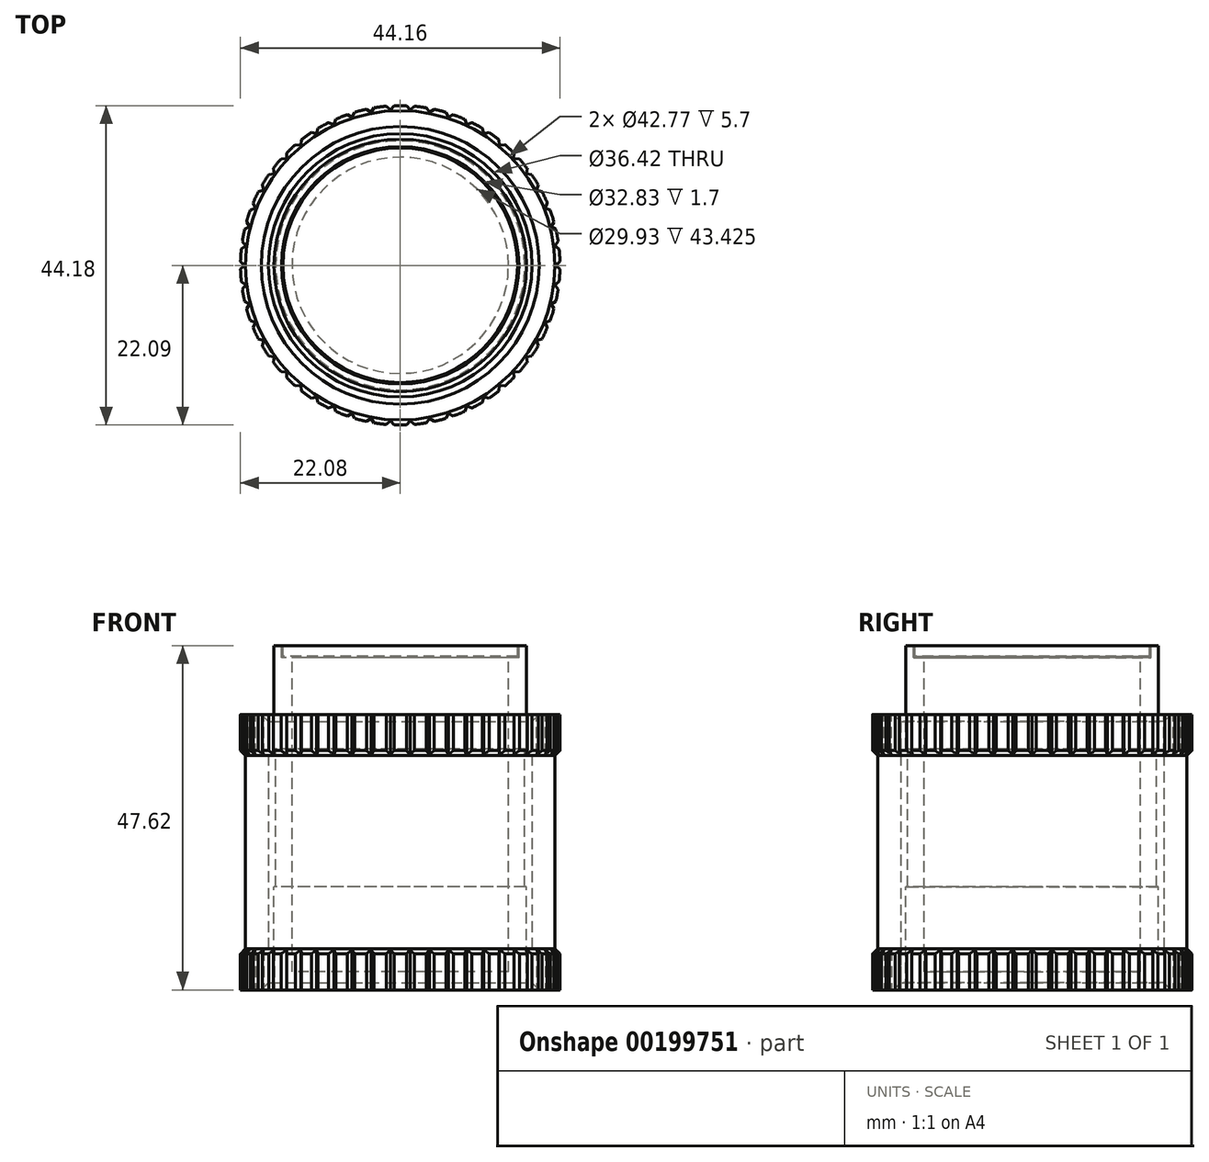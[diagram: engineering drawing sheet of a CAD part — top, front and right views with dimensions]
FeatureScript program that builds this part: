
annotation { "Feature Type Name" : "Feature", "Feature Type Description" : "" }
export const myFeature = defineFeature(function(context is Context, id is Id, definition is map)
    precondition{}
    {
        {
            var Q0;
            Q0=qCreatedBy(makeId("Front.planeOp"),FACE);
            var sketch = newSketch(context, id + "F0", { "sketchPlane" : qUnion([Q0])});
            skLineSegment(sketch, "E0", {"start": v(0, 33.65) * mm, "end": v(0, -36.31) * mm, "construction": true});
            skLineSegment(sketch, "E1", {"start": v(0, 23.81) * mm, "end": v(-17.46, 23.81) * mm});
            skLineSegment(sketch, "E2", {"start": v(-17.46, 23.81) * mm, "end": v(-17.46, -23.81) * mm});
            skLineSegment(sketch, "E3", {"start": v(-17.46, -23.81) * mm, "end": v(0, -23.81) * mm});
            skPoint(sketch, "E4", {"position": v(-17.46, 0) * mm});
            skLineSegment(sketch, "E5.bottom", {"start": v(-17.46, 9.53) * mm, "end": v(-17.21, 9.53) * mm});
            skLineSegment(sketch, "E5.top", {"start": v(-17.46, -9.52) * mm, "end": v(-17.21, -9.52) * mm});
            skLineSegment(sketch, "E5.left", {"start": v(-17.46, 9.52) * mm, "end": v(-17.46, -9.52) * mm});
            skLineSegment(sketch, "E5.right", {"start": v(-17.21, 9.52) * mm, "end": v(-17.21, -9.52) * mm});
            skLineSegment(sketch, "E6", {"start": v(-14.96, 23.81) * mm, "end": v(-14.96, -21.31) * mm});
            skLineSegment(sketch, "E7", {"start": v(-14.96, -21.31) * mm, "end": v(0, -21.31) * mm});
            skPoint(sketch, "E7.endSnap0", {"position": v(0, -1.33) * mm});
            skLineSegment(sketch, "E8", {"start": v(0, -23.81) * mm, "end": v(0, -21.31) * mm});
            skSolve(sketch);
        }
        {
            var Q0;
            {var subQ0=sQuery(id+"F0.wireOp",EDGE,"E3");Q0=makeQuery(id+"F0.imprint","IMPRINT",FACE,{"disambiguationData":[TD([[makeQuery(id+"F0.imprint","IMPRINT",EDGE,{"derivedFrom":subQ0}),1.0]])]});}
            var Q1;
            Q1=sQuery(id+"F0.wireOp",EDGE,"E0");
            revolve(context, id + "F1", {"entities" : qUnion([Q0]), "axis" : qUnion([Q1]), "revolveType" : RevolveType.FULL});
        }
        {
            var Q0;
            Q0=makeQuery(id+"F1.opRevolve","SWEPT_FACE",FACE,{"disambiguationData":[OSD([sQuery(id+"F0.wireOp",EDGE,"E1")])]});
            cPlane(context, id + "F2", {"entities" : qUnion([Q0]), "cplaneType" : CPlaneType.OFFSET, "offset" : 0 * mm, "width" : 150 * mm, "height" : 150 * mm});
        }
        {
            var Q0;
            Q0=qCreatedBy(id+"F2.planeOp",FACE);
            var sketch = newSketch(context, id + "F3", { "sketchPlane" : qUnion([Q0])});
            skCircle(sketch, "E9", {"center": v(0, 0) * mm, "radius": 16.21 * mm});
            skPoint(sketch, "E10", {"position": v(-17.46, 0) * mm});
            skSolve(sketch);
        }
        {
            var Q0;
            Q0 = qSketchRegion(id + "F3", true);
            extrude(context, id + "F4", {"entities" : qUnion([Q0]), "oppositeDirection" : true, "depth" : 1.5 * mm});
        }
        {
            var Q0;
            Q0=makeQuery(id+"F4.opExtrude","SWEPT_BODY",BODY,{"disambiguationData":[OSD([sQuery(id+"F3.wireOp",EDGE,"E9")])]});
            var Q1;
            Q1=makeQuery(id+"F1.opRevolve","SWEPT_BODY",BODY,{"disambiguationData":[OSD([sQuery(id+"F0.wireOp",EDGE,"E1"),sQuery(id+"F0.wireOp",EDGE,"E2"),sQuery(id+"F0.wireOp",EDGE,"E3"),sQuery(id+"F0.wireOp",EDGE,"E5.bottom"),sQuery(id+"F0.wireOp",EDGE,"E5.top"),sQuery(id+"F0.wireOp",EDGE,"E5.right"),sQuery(id+"F0.wireOp",EDGE,"E6"),sQuery(id+"F0.wireOp",EDGE,"E7"),sQuery(id+"F0.wireOp",EDGE,"E8")])]});
            booleanBodies(context, id + "F5", {"operationType" : BooleanOperationType.SUBTRACTION, "tools" : qUnion([Q0]), "targets" : qUnion([Q1]), "offset" : true, "offsetAll" : true, "offsetDistance" : .2 * mm, "keepTools" : true});
        }
        {
            var Q0;
            Q0=makeQuery(id+"F1.opRevolve","SWEPT_FACE",FACE,{"disambiguationData":[OSD([sQuery(id+"F0.wireOp",EDGE,"E3")])]});
            cPlane(context, id + "F6", {"entities" : qUnion([Q0]), "cplaneType" : CPlaneType.OFFSET, "offset" : 0 * mm, "width" : 150 * mm, "height" : 150 * mm});
        }
        {
            var Q0;
            Q0=qCreatedBy(id+"F6.planeOp",FACE);
            var sketch = newSketch(context, id + "F7", { "sketchPlane" : qUnion([Q0])});
            skCircle(sketch, "E11", {"center": v(0, 0) * mm, "radius": 18.21 * mm});
            skCircle(sketch, "E12", {"center": v(0, 0) * mm, "radius": 21.39 * mm});
            skSolve(sketch);
        }
        {
            var Q0;
            Q0=makeQuery(id+"F7.imprint","IMPRINT",FACE,{"disambiguationData":[TD([[makeQuery(id+"F7.imprint","IMPRINT",EDGE,{"derivedFrom":sQuery(id+"F7.wireOp",EDGE,"E11")}),-1.0]])]});
            extrude(context, id + "F8", {"entities" : qUnion([Q0]), "oppositeDirection" : true, "depth" : 38.1 * mm, "offsetDistance" : 25 * mm});
        }
        {
            var Q0;
            Q0=qCreatedBy(makeId("Front.planeOp"),FACE);
            var sketch = newSketch(context, id + "F9", { "sketchPlane" : qUnion([Q0])});
            skLineSegment(sketch, "E13", {"start": v(-21.39, -23.81) * mm, "end": v(-21.39, 14.29) * mm});
            skLineSegment(sketch, "E14.0", {"start": v(21.39, 14.29) * mm, "end": v(-21.39, 14.29) * mm});
            skLineSegment(sketch, "E15", {"start": v(-21.39, 14.29) * mm, "end": v(-22.09, 14.29) * mm});
            skLineSegment(sketch, "E16", {"start": v(-22.09, 14.29) * mm, "end": v(-22.09, 9.29) * mm});
            skLineSegment(sketch, "E17", {"start": v(-22.09, 9.29) * mm, "end": v(-21.39, 8.59) * mm});
            skLineSegment(sketch, "E18", {"start": v(0, 29.24) * mm, "end": v(0, -34.18) * mm, "construction": true});
            skLineSegment(sketch, "E19", {"start": v(-37.39, -4.76) * mm, "end": v(45.58, -4.76) * mm, "construction": true});
            skPoint(sketch, "E20", {"position": v(-21.39, -4.76) * mm});
            skSolve(sketch);
        }
        {
            var Q0;
            {var subQ0=sQuery(id+"F9.wireOp",EDGE,"E15");Q0=makeQuery(id+"F9.imprint","IMPRINT",FACE,{"disambiguationData":[TD([[makeQuery(id+"F9.imprint","IMPRINT",EDGE,{"derivedFrom":subQ0}),1.0]])]});}
            var Q1;
            Q1=sQuery(id+"F9.wireOp",EDGE,"E18");
            revolve(context, id + "F10", {"surfaceOperationType" : NewSurfaceOperationType.NEW, "entities" : qUnion([Q0]), "axis" : qUnion([Q1]), "revolveType" : RevolveType.FULL});
        }
        {
            var Q0;
            Q0=qCreatedBy(makeId("Top.planeOp"),FACE);
            var Q1;
            Q1=sQuery(id+"F9.wireOp",VERTEX,"E20");
            cPlane(context, id + "F11", {"entities" : qUnion([Q0, Q1]), "cplaneType" : CPlaneType.PLANE_POINT, "offset" : 25 * mm, "width" : 150 * mm, "height" : 150 * mm});
        }
        {
            var Q0;
            Q0=makeQuery(id+"F10.opRevolve","SWEPT_FACE",FACE,{"disambiguationData":[OSD([sQuery(id+"F9.wireOp",EDGE,"E15")])]});
            cPlane(context, id + "F12", {"entities" : qUnion([Q0]), "cplaneType" : CPlaneType.OFFSET, "offset" : 0 * mm, "width" : 150 * mm, "height" : 150 * mm});
        }
        {
            var Q0;
            Q0=qCreatedBy(id+"F12.planeOp",FACE);
            var sketch = newSketch(context, id + "F13", { "sketchPlane" : qUnion([Q0])});
            skLineSegment(sketch, "E21", {"start": v(27.17, 0) * mm, "end": v(-30.77, 0) * mm, "construction": true});
            skLineSegment(sketch, "E22.bottom", {"start": v(-22.6, 1.06) * mm, "end": v(-21.54, 0) * mm});
            skLineSegment(sketch, "E22.top", {"start": v(-23.66, 0) * mm, "end": v(-22.6, -1.06) * mm});
            skLineSegment(sketch, "E22.left", {"start": v(-22.6, 1.06) * mm, "end": v(-23.66, 0) * mm});
            skLineSegment(sketch, "E22.right", {"start": v(-21.54, 0) * mm, "end": v(-22.6, -1.06) * mm});
            skPoint(sketch, "E23", {"position": v(-22.09, 0) * mm});
            skSolve(sketch);
        }
        {
            var Q0;
            Q0=makeQuery(id+"F13.imprint","IMPRINT",FACE,{"disambiguationData":[TD([[makeQuery(id+"F13.imprint","IMPRINT",EDGE,{"derivedFrom":sQuery(id+"F13.wireOp",EDGE,"E22.bottom")}),-1.0]])]});
            var Q1;
            Q1=makeQuery(id+"F10.opRevolve","SWEPT_FACE",FACE,{"disambiguationData":[OSD([sQuery(id+"F9.wireOp",EDGE,"E17")])]});
            extrude(context, id + "F14", {"entities" : qUnion([Q0]), "endBound" : BoundingType.UP_TO_SURFACE, "oppositeDirection" : true, "depth" : 25 * mm, "endBoundEntityFace" : qUnion([Q1]), "offsetDistance" : 25 * mm});
        }
        {
            var Q0;
            Q0=qCreatedBy(makeId("Front.planeOp"),FACE);
            var sketch = newSketch(context, id + "F15", { "sketchPlane" : qUnion([Q0])});
            skLineSegment(sketch, "E24", {"start": v(0, 30.02) * mm, "end": v(0, -34.27) * mm, "construction": true});
            skSolve(sketch);
        }
        {
            var Q0;
            Q0=makeQuery(id+"F14.opExtrude","SWEPT_BODY",BODY,{"disambiguationData":[OSD([sQuery(id+"F13.wireOp",EDGE,"E22.bottom"),sQuery(id+"F13.wireOp",EDGE,"E22.top"),sQuery(id+"F13.wireOp",EDGE,"E22.left"),sQuery(id+"F13.wireOp",EDGE,"E22.right")])]});
            var Q1;
            Q1=sQuery(id+"F15.wireOp",EDGE,"E24");
            circularPattern(context, id + "F16", {"entities" : qUnion([Q0]), "axis" : qUnion([Q1]), "angle" : 360 * degree, "instanceCount" : 50, "equalSpace" : true});
        }
        {
            var Q0;
            Q0=makeQuery(id+"F14.opExtrude","SWEPT_BODY",BODY,{"disambiguationData":[OSD([sQuery(id+"F13.wireOp",EDGE,"E22.bottom"),sQuery(id+"F13.wireOp",EDGE,"E22.top"),sQuery(id+"F13.wireOp",EDGE,"E22.left"),sQuery(id+"F13.wireOp",EDGE,"E22.right")])]});
            var Q1;
            Q1=makeQuery(id+"F16.opPattern","COPY",BODY,{"derivedFrom":makeQuery(id+"F14.opExtrude","SWEPT_BODY",BODY,{"disambiguationData":[OSD([sQuery(id+"F13.wireOp",EDGE,"E22.bottom"),sQuery(id+"F13.wireOp",EDGE,"E22.top"),sQuery(id+"F13.wireOp",EDGE,"E22.left"),sQuery(id+"F13.wireOp",EDGE,"E22.right")])]}),"instanceName":"1"});
            var Q2;
            Q2=makeQuery(id+"F16.opPattern","COPY",BODY,{"derivedFrom":makeQuery(id+"F14.opExtrude","SWEPT_BODY",BODY,{"disambiguationData":[OSD([sQuery(id+"F13.wireOp",EDGE,"E22.bottom"),sQuery(id+"F13.wireOp",EDGE,"E22.top"),sQuery(id+"F13.wireOp",EDGE,"E22.left"),sQuery(id+"F13.wireOp",EDGE,"E22.right")])]}),"instanceName":"2"});
            var Q3;
            Q3=makeQuery(id+"F16.opPattern","COPY",BODY,{"derivedFrom":makeQuery(id+"F14.opExtrude","SWEPT_BODY",BODY,{"disambiguationData":[OSD([sQuery(id+"F13.wireOp",EDGE,"E22.bottom"),sQuery(id+"F13.wireOp",EDGE,"E22.top"),sQuery(id+"F13.wireOp",EDGE,"E22.left"),sQuery(id+"F13.wireOp",EDGE,"E22.right")])]}),"instanceName":"3"});
            var Q4;
            Q4=makeQuery(id+"F16.opPattern","COPY",BODY,{"derivedFrom":makeQuery(id+"F14.opExtrude","SWEPT_BODY",BODY,{"disambiguationData":[OSD([sQuery(id+"F13.wireOp",EDGE,"E22.bottom"),sQuery(id+"F13.wireOp",EDGE,"E22.top"),sQuery(id+"F13.wireOp",EDGE,"E22.left"),sQuery(id+"F13.wireOp",EDGE,"E22.right")])]}),"instanceName":"4"});
            var Q5;
            Q5=makeQuery(id+"F16.opPattern","COPY",BODY,{"derivedFrom":makeQuery(id+"F14.opExtrude","SWEPT_BODY",BODY,{"disambiguationData":[OSD([sQuery(id+"F13.wireOp",EDGE,"E22.bottom"),sQuery(id+"F13.wireOp",EDGE,"E22.top"),sQuery(id+"F13.wireOp",EDGE,"E22.left"),sQuery(id+"F13.wireOp",EDGE,"E22.right")])]}),"instanceName":"5"});
            var Q6;
            Q6=makeQuery(id+"F16.opPattern","COPY",BODY,{"derivedFrom":makeQuery(id+"F14.opExtrude","SWEPT_BODY",BODY,{"disambiguationData":[OSD([sQuery(id+"F13.wireOp",EDGE,"E22.bottom"),sQuery(id+"F13.wireOp",EDGE,"E22.top"),sQuery(id+"F13.wireOp",EDGE,"E22.left"),sQuery(id+"F13.wireOp",EDGE,"E22.right")])]}),"instanceName":"6"});
            var Q7;
            Q7=makeQuery(id+"F16.opPattern","COPY",BODY,{"derivedFrom":makeQuery(id+"F14.opExtrude","SWEPT_BODY",BODY,{"disambiguationData":[OSD([sQuery(id+"F13.wireOp",EDGE,"E22.bottom"),sQuery(id+"F13.wireOp",EDGE,"E22.top"),sQuery(id+"F13.wireOp",EDGE,"E22.left"),sQuery(id+"F13.wireOp",EDGE,"E22.right")])]}),"instanceName":"7"});
            var Q8;
            Q8=makeQuery(id+"F16.opPattern","COPY",BODY,{"derivedFrom":makeQuery(id+"F14.opExtrude","SWEPT_BODY",BODY,{"disambiguationData":[OSD([sQuery(id+"F13.wireOp",EDGE,"E22.bottom"),sQuery(id+"F13.wireOp",EDGE,"E22.top"),sQuery(id+"F13.wireOp",EDGE,"E22.left"),sQuery(id+"F13.wireOp",EDGE,"E22.right")])]}),"instanceName":"8"});
            var Q9;
            Q9=makeQuery(id+"F16.opPattern","COPY",BODY,{"derivedFrom":makeQuery(id+"F14.opExtrude","SWEPT_BODY",BODY,{"disambiguationData":[OSD([sQuery(id+"F13.wireOp",EDGE,"E22.bottom"),sQuery(id+"F13.wireOp",EDGE,"E22.top"),sQuery(id+"F13.wireOp",EDGE,"E22.left"),sQuery(id+"F13.wireOp",EDGE,"E22.right")])]}),"instanceName":"9"});
            var Q10;
            Q10=makeQuery(id+"F16.opPattern","COPY",BODY,{"derivedFrom":makeQuery(id+"F14.opExtrude","SWEPT_BODY",BODY,{"disambiguationData":[OSD([sQuery(id+"F13.wireOp",EDGE,"E22.bottom"),sQuery(id+"F13.wireOp",EDGE,"E22.top"),sQuery(id+"F13.wireOp",EDGE,"E22.left"),sQuery(id+"F13.wireOp",EDGE,"E22.right")])]}),"instanceName":"10"});
            var Q11;
            Q11=makeQuery(id+"F16.opPattern","COPY",BODY,{"derivedFrom":makeQuery(id+"F14.opExtrude","SWEPT_BODY",BODY,{"disambiguationData":[OSD([sQuery(id+"F13.wireOp",EDGE,"E22.bottom"),sQuery(id+"F13.wireOp",EDGE,"E22.top"),sQuery(id+"F13.wireOp",EDGE,"E22.left"),sQuery(id+"F13.wireOp",EDGE,"E22.right")])]}),"instanceName":"11"});
            var Q12;
            Q12=makeQuery(id+"F16.opPattern","COPY",BODY,{"derivedFrom":makeQuery(id+"F14.opExtrude","SWEPT_BODY",BODY,{"disambiguationData":[OSD([sQuery(id+"F13.wireOp",EDGE,"E22.bottom"),sQuery(id+"F13.wireOp",EDGE,"E22.top"),sQuery(id+"F13.wireOp",EDGE,"E22.left"),sQuery(id+"F13.wireOp",EDGE,"E22.right")])]}),"instanceName":"12"});
            var Q13;
            Q13=makeQuery(id+"F16.opPattern","COPY",BODY,{"derivedFrom":makeQuery(id+"F14.opExtrude","SWEPT_BODY",BODY,{"disambiguationData":[OSD([sQuery(id+"F13.wireOp",EDGE,"E22.bottom"),sQuery(id+"F13.wireOp",EDGE,"E22.top"),sQuery(id+"F13.wireOp",EDGE,"E22.left"),sQuery(id+"F13.wireOp",EDGE,"E22.right")])]}),"instanceName":"13"});
            var Q14;
            Q14=makeQuery(id+"F16.opPattern","COPY",BODY,{"derivedFrom":makeQuery(id+"F14.opExtrude","SWEPT_BODY",BODY,{"disambiguationData":[OSD([sQuery(id+"F13.wireOp",EDGE,"E22.bottom"),sQuery(id+"F13.wireOp",EDGE,"E22.top"),sQuery(id+"F13.wireOp",EDGE,"E22.left"),sQuery(id+"F13.wireOp",EDGE,"E22.right")])]}),"instanceName":"14"});
            var Q15;
            Q15=makeQuery(id+"F16.opPattern","COPY",BODY,{"derivedFrom":makeQuery(id+"F14.opExtrude","SWEPT_BODY",BODY,{"disambiguationData":[OSD([sQuery(id+"F13.wireOp",EDGE,"E22.bottom"),sQuery(id+"F13.wireOp",EDGE,"E22.top"),sQuery(id+"F13.wireOp",EDGE,"E22.left"),sQuery(id+"F13.wireOp",EDGE,"E22.right")])]}),"instanceName":"15"});
            var Q16;
            Q16=makeQuery(id+"F16.opPattern","COPY",BODY,{"derivedFrom":makeQuery(id+"F14.opExtrude","SWEPT_BODY",BODY,{"disambiguationData":[OSD([sQuery(id+"F13.wireOp",EDGE,"E22.bottom"),sQuery(id+"F13.wireOp",EDGE,"E22.top"),sQuery(id+"F13.wireOp",EDGE,"E22.left"),sQuery(id+"F13.wireOp",EDGE,"E22.right")])]}),"instanceName":"16"});
            var Q17;
            Q17=makeQuery(id+"F16.opPattern","COPY",BODY,{"derivedFrom":makeQuery(id+"F14.opExtrude","SWEPT_BODY",BODY,{"disambiguationData":[OSD([sQuery(id+"F13.wireOp",EDGE,"E22.bottom"),sQuery(id+"F13.wireOp",EDGE,"E22.top"),sQuery(id+"F13.wireOp",EDGE,"E22.left"),sQuery(id+"F13.wireOp",EDGE,"E22.right")])]}),"instanceName":"17"});
            var Q18;
            Q18=makeQuery(id+"F16.opPattern","COPY",BODY,{"derivedFrom":makeQuery(id+"F14.opExtrude","SWEPT_BODY",BODY,{"disambiguationData":[OSD([sQuery(id+"F13.wireOp",EDGE,"E22.bottom"),sQuery(id+"F13.wireOp",EDGE,"E22.top"),sQuery(id+"F13.wireOp",EDGE,"E22.left"),sQuery(id+"F13.wireOp",EDGE,"E22.right")])]}),"instanceName":"18"});
            var Q19;
            Q19=makeQuery(id+"F16.opPattern","COPY",BODY,{"derivedFrom":makeQuery(id+"F14.opExtrude","SWEPT_BODY",BODY,{"disambiguationData":[OSD([sQuery(id+"F13.wireOp",EDGE,"E22.bottom"),sQuery(id+"F13.wireOp",EDGE,"E22.top"),sQuery(id+"F13.wireOp",EDGE,"E22.left"),sQuery(id+"F13.wireOp",EDGE,"E22.right")])]}),"instanceName":"19"});
            var Q20;
            Q20=makeQuery(id+"F16.opPattern","COPY",BODY,{"derivedFrom":makeQuery(id+"F14.opExtrude","SWEPT_BODY",BODY,{"disambiguationData":[OSD([sQuery(id+"F13.wireOp",EDGE,"E22.bottom"),sQuery(id+"F13.wireOp",EDGE,"E22.top"),sQuery(id+"F13.wireOp",EDGE,"E22.left"),sQuery(id+"F13.wireOp",EDGE,"E22.right")])]}),"instanceName":"20"});
            var Q21;
            Q21=makeQuery(id+"F16.opPattern","COPY",BODY,{"derivedFrom":makeQuery(id+"F14.opExtrude","SWEPT_BODY",BODY,{"disambiguationData":[OSD([sQuery(id+"F13.wireOp",EDGE,"E22.bottom"),sQuery(id+"F13.wireOp",EDGE,"E22.top"),sQuery(id+"F13.wireOp",EDGE,"E22.left"),sQuery(id+"F13.wireOp",EDGE,"E22.right")])]}),"instanceName":"21"});
            var Q22;
            Q22=makeQuery(id+"F16.opPattern","COPY",BODY,{"derivedFrom":makeQuery(id+"F14.opExtrude","SWEPT_BODY",BODY,{"disambiguationData":[OSD([sQuery(id+"F13.wireOp",EDGE,"E22.bottom"),sQuery(id+"F13.wireOp",EDGE,"E22.top"),sQuery(id+"F13.wireOp",EDGE,"E22.left"),sQuery(id+"F13.wireOp",EDGE,"E22.right")])]}),"instanceName":"22"});
            var Q23;
            Q23=makeQuery(id+"F16.opPattern","COPY",BODY,{"derivedFrom":makeQuery(id+"F14.opExtrude","SWEPT_BODY",BODY,{"disambiguationData":[OSD([sQuery(id+"F13.wireOp",EDGE,"E22.bottom"),sQuery(id+"F13.wireOp",EDGE,"E22.top"),sQuery(id+"F13.wireOp",EDGE,"E22.left"),sQuery(id+"F13.wireOp",EDGE,"E22.right")])]}),"instanceName":"23"});
            var Q24;
            Q24=makeQuery(id+"F16.opPattern","COPY",BODY,{"derivedFrom":makeQuery(id+"F14.opExtrude","SWEPT_BODY",BODY,{"disambiguationData":[OSD([sQuery(id+"F13.wireOp",EDGE,"E22.bottom"),sQuery(id+"F13.wireOp",EDGE,"E22.top"),sQuery(id+"F13.wireOp",EDGE,"E22.left"),sQuery(id+"F13.wireOp",EDGE,"E22.right")])]}),"instanceName":"24"});
            var Q25;
            Q25=makeQuery(id+"F16.opPattern","COPY",BODY,{"derivedFrom":makeQuery(id+"F14.opExtrude","SWEPT_BODY",BODY,{"disambiguationData":[OSD([sQuery(id+"F13.wireOp",EDGE,"E22.bottom"),sQuery(id+"F13.wireOp",EDGE,"E22.top"),sQuery(id+"F13.wireOp",EDGE,"E22.left"),sQuery(id+"F13.wireOp",EDGE,"E22.right")])]}),"instanceName":"25"});
            var Q26;
            Q26=makeQuery(id+"F16.opPattern","COPY",BODY,{"derivedFrom":makeQuery(id+"F14.opExtrude","SWEPT_BODY",BODY,{"disambiguationData":[OSD([sQuery(id+"F13.wireOp",EDGE,"E22.bottom"),sQuery(id+"F13.wireOp",EDGE,"E22.top"),sQuery(id+"F13.wireOp",EDGE,"E22.left"),sQuery(id+"F13.wireOp",EDGE,"E22.right")])]}),"instanceName":"26"});
            var Q27;
            Q27=makeQuery(id+"F16.opPattern","COPY",BODY,{"derivedFrom":makeQuery(id+"F14.opExtrude","SWEPT_BODY",BODY,{"disambiguationData":[OSD([sQuery(id+"F13.wireOp",EDGE,"E22.bottom"),sQuery(id+"F13.wireOp",EDGE,"E22.top"),sQuery(id+"F13.wireOp",EDGE,"E22.left"),sQuery(id+"F13.wireOp",EDGE,"E22.right")])]}),"instanceName":"27"});
            var Q28;
            Q28=makeQuery(id+"F16.opPattern","COPY",BODY,{"derivedFrom":makeQuery(id+"F14.opExtrude","SWEPT_BODY",BODY,{"disambiguationData":[OSD([sQuery(id+"F13.wireOp",EDGE,"E22.bottom"),sQuery(id+"F13.wireOp",EDGE,"E22.top"),sQuery(id+"F13.wireOp",EDGE,"E22.left"),sQuery(id+"F13.wireOp",EDGE,"E22.right")])]}),"instanceName":"28"});
            var Q29;
            Q29=makeQuery(id+"F16.opPattern","COPY",BODY,{"derivedFrom":makeQuery(id+"F14.opExtrude","SWEPT_BODY",BODY,{"disambiguationData":[OSD([sQuery(id+"F13.wireOp",EDGE,"E22.bottom"),sQuery(id+"F13.wireOp",EDGE,"E22.top"),sQuery(id+"F13.wireOp",EDGE,"E22.left"),sQuery(id+"F13.wireOp",EDGE,"E22.right")])]}),"instanceName":"29"});
            var Q30;
            Q30=makeQuery(id+"F16.opPattern","COPY",BODY,{"derivedFrom":makeQuery(id+"F14.opExtrude","SWEPT_BODY",BODY,{"disambiguationData":[OSD([sQuery(id+"F13.wireOp",EDGE,"E22.bottom"),sQuery(id+"F13.wireOp",EDGE,"E22.top"),sQuery(id+"F13.wireOp",EDGE,"E22.left"),sQuery(id+"F13.wireOp",EDGE,"E22.right")])]}),"instanceName":"30"});
            var Q31;
            Q31=makeQuery(id+"F16.opPattern","COPY",BODY,{"derivedFrom":makeQuery(id+"F14.opExtrude","SWEPT_BODY",BODY,{"disambiguationData":[OSD([sQuery(id+"F13.wireOp",EDGE,"E22.bottom"),sQuery(id+"F13.wireOp",EDGE,"E22.top"),sQuery(id+"F13.wireOp",EDGE,"E22.left"),sQuery(id+"F13.wireOp",EDGE,"E22.right")])]}),"instanceName":"31"});
            var Q32;
            Q32=makeQuery(id+"F16.opPattern","COPY",BODY,{"derivedFrom":makeQuery(id+"F14.opExtrude","SWEPT_BODY",BODY,{"disambiguationData":[OSD([sQuery(id+"F13.wireOp",EDGE,"E22.bottom"),sQuery(id+"F13.wireOp",EDGE,"E22.top"),sQuery(id+"F13.wireOp",EDGE,"E22.left"),sQuery(id+"F13.wireOp",EDGE,"E22.right")])]}),"instanceName":"32"});
            var Q33;
            Q33=makeQuery(id+"F16.opPattern","COPY",BODY,{"derivedFrom":makeQuery(id+"F14.opExtrude","SWEPT_BODY",BODY,{"disambiguationData":[OSD([sQuery(id+"F13.wireOp",EDGE,"E22.bottom"),sQuery(id+"F13.wireOp",EDGE,"E22.top"),sQuery(id+"F13.wireOp",EDGE,"E22.left"),sQuery(id+"F13.wireOp",EDGE,"E22.right")])]}),"instanceName":"33"});
            var Q34;
            Q34=makeQuery(id+"F16.opPattern","COPY",BODY,{"derivedFrom":makeQuery(id+"F14.opExtrude","SWEPT_BODY",BODY,{"disambiguationData":[OSD([sQuery(id+"F13.wireOp",EDGE,"E22.bottom"),sQuery(id+"F13.wireOp",EDGE,"E22.top"),sQuery(id+"F13.wireOp",EDGE,"E22.left"),sQuery(id+"F13.wireOp",EDGE,"E22.right")])]}),"instanceName":"34"});
            var Q35;
            Q35=makeQuery(id+"F16.opPattern","COPY",BODY,{"derivedFrom":makeQuery(id+"F14.opExtrude","SWEPT_BODY",BODY,{"disambiguationData":[OSD([sQuery(id+"F13.wireOp",EDGE,"E22.bottom"),sQuery(id+"F13.wireOp",EDGE,"E22.top"),sQuery(id+"F13.wireOp",EDGE,"E22.left"),sQuery(id+"F13.wireOp",EDGE,"E22.right")])]}),"instanceName":"35"});
            var Q36;
            Q36=makeQuery(id+"F16.opPattern","COPY",BODY,{"derivedFrom":makeQuery(id+"F14.opExtrude","SWEPT_BODY",BODY,{"disambiguationData":[OSD([sQuery(id+"F13.wireOp",EDGE,"E22.bottom"),sQuery(id+"F13.wireOp",EDGE,"E22.top"),sQuery(id+"F13.wireOp",EDGE,"E22.left"),sQuery(id+"F13.wireOp",EDGE,"E22.right")])]}),"instanceName":"36"});
            var Q37;
            Q37=makeQuery(id+"F16.opPattern","COPY",BODY,{"derivedFrom":makeQuery(id+"F14.opExtrude","SWEPT_BODY",BODY,{"disambiguationData":[OSD([sQuery(id+"F13.wireOp",EDGE,"E22.bottom"),sQuery(id+"F13.wireOp",EDGE,"E22.top"),sQuery(id+"F13.wireOp",EDGE,"E22.left"),sQuery(id+"F13.wireOp",EDGE,"E22.right")])]}),"instanceName":"37"});
            var Q38;
            Q38=makeQuery(id+"F16.opPattern","COPY",BODY,{"derivedFrom":makeQuery(id+"F14.opExtrude","SWEPT_BODY",BODY,{"disambiguationData":[OSD([sQuery(id+"F13.wireOp",EDGE,"E22.bottom"),sQuery(id+"F13.wireOp",EDGE,"E22.top"),sQuery(id+"F13.wireOp",EDGE,"E22.left"),sQuery(id+"F13.wireOp",EDGE,"E22.right")])]}),"instanceName":"38"});
            var Q39;
            Q39=makeQuery(id+"F16.opPattern","COPY",BODY,{"derivedFrom":makeQuery(id+"F14.opExtrude","SWEPT_BODY",BODY,{"disambiguationData":[OSD([sQuery(id+"F13.wireOp",EDGE,"E22.bottom"),sQuery(id+"F13.wireOp",EDGE,"E22.top"),sQuery(id+"F13.wireOp",EDGE,"E22.left"),sQuery(id+"F13.wireOp",EDGE,"E22.right")])]}),"instanceName":"39"});
            var Q40;
            Q40=makeQuery(id+"F16.opPattern","COPY",BODY,{"derivedFrom":makeQuery(id+"F14.opExtrude","SWEPT_BODY",BODY,{"disambiguationData":[OSD([sQuery(id+"F13.wireOp",EDGE,"E22.bottom"),sQuery(id+"F13.wireOp",EDGE,"E22.top"),sQuery(id+"F13.wireOp",EDGE,"E22.left"),sQuery(id+"F13.wireOp",EDGE,"E22.right")])]}),"instanceName":"40"});
            var Q41;
            Q41=makeQuery(id+"F16.opPattern","COPY",BODY,{"derivedFrom":makeQuery(id+"F14.opExtrude","SWEPT_BODY",BODY,{"disambiguationData":[OSD([sQuery(id+"F13.wireOp",EDGE,"E22.bottom"),sQuery(id+"F13.wireOp",EDGE,"E22.top"),sQuery(id+"F13.wireOp",EDGE,"E22.left"),sQuery(id+"F13.wireOp",EDGE,"E22.right")])]}),"instanceName":"41"});
            var Q42;
            Q42=makeQuery(id+"F16.opPattern","COPY",BODY,{"derivedFrom":makeQuery(id+"F14.opExtrude","SWEPT_BODY",BODY,{"disambiguationData":[OSD([sQuery(id+"F13.wireOp",EDGE,"E22.bottom"),sQuery(id+"F13.wireOp",EDGE,"E22.top"),sQuery(id+"F13.wireOp",EDGE,"E22.left"),sQuery(id+"F13.wireOp",EDGE,"E22.right")])]}),"instanceName":"42"});
            var Q43;
            Q43=makeQuery(id+"F16.opPattern","COPY",BODY,{"derivedFrom":makeQuery(id+"F14.opExtrude","SWEPT_BODY",BODY,{"disambiguationData":[OSD([sQuery(id+"F13.wireOp",EDGE,"E22.bottom"),sQuery(id+"F13.wireOp",EDGE,"E22.top"),sQuery(id+"F13.wireOp",EDGE,"E22.left"),sQuery(id+"F13.wireOp",EDGE,"E22.right")])]}),"instanceName":"43"});
            var Q44;
            Q44=makeQuery(id+"F16.opPattern","COPY",BODY,{"derivedFrom":makeQuery(id+"F14.opExtrude","SWEPT_BODY",BODY,{"disambiguationData":[OSD([sQuery(id+"F13.wireOp",EDGE,"E22.bottom"),sQuery(id+"F13.wireOp",EDGE,"E22.top"),sQuery(id+"F13.wireOp",EDGE,"E22.left"),sQuery(id+"F13.wireOp",EDGE,"E22.right")])]}),"instanceName":"44"});
            var Q45;
            Q45=makeQuery(id+"F16.opPattern","COPY",BODY,{"derivedFrom":makeQuery(id+"F14.opExtrude","SWEPT_BODY",BODY,{"disambiguationData":[OSD([sQuery(id+"F13.wireOp",EDGE,"E22.bottom"),sQuery(id+"F13.wireOp",EDGE,"E22.top"),sQuery(id+"F13.wireOp",EDGE,"E22.left"),sQuery(id+"F13.wireOp",EDGE,"E22.right")])]}),"instanceName":"45"});
            var Q46;
            Q46=makeQuery(id+"F16.opPattern","COPY",BODY,{"derivedFrom":makeQuery(id+"F14.opExtrude","SWEPT_BODY",BODY,{"disambiguationData":[OSD([sQuery(id+"F13.wireOp",EDGE,"E22.bottom"),sQuery(id+"F13.wireOp",EDGE,"E22.top"),sQuery(id+"F13.wireOp",EDGE,"E22.left"),sQuery(id+"F13.wireOp",EDGE,"E22.right")])]}),"instanceName":"46"});
            var Q47;
            Q47=makeQuery(id+"F16.opPattern","COPY",BODY,{"derivedFrom":makeQuery(id+"F14.opExtrude","SWEPT_BODY",BODY,{"disambiguationData":[OSD([sQuery(id+"F13.wireOp",EDGE,"E22.bottom"),sQuery(id+"F13.wireOp",EDGE,"E22.top"),sQuery(id+"F13.wireOp",EDGE,"E22.left"),sQuery(id+"F13.wireOp",EDGE,"E22.right")])]}),"instanceName":"47"});
            var Q48;
            Q48=makeQuery(id+"F16.opPattern","COPY",BODY,{"derivedFrom":makeQuery(id+"F14.opExtrude","SWEPT_BODY",BODY,{"disambiguationData":[OSD([sQuery(id+"F13.wireOp",EDGE,"E22.bottom"),sQuery(id+"F13.wireOp",EDGE,"E22.top"),sQuery(id+"F13.wireOp",EDGE,"E22.left"),sQuery(id+"F13.wireOp",EDGE,"E22.right")])]}),"instanceName":"48"});
            var Q49;
            Q49=makeQuery(id+"F16.opPattern","COPY",BODY,{"derivedFrom":makeQuery(id+"F14.opExtrude","SWEPT_BODY",BODY,{"disambiguationData":[OSD([sQuery(id+"F13.wireOp",EDGE,"E22.bottom"),sQuery(id+"F13.wireOp",EDGE,"E22.top"),sQuery(id+"F13.wireOp",EDGE,"E22.left"),sQuery(id+"F13.wireOp",EDGE,"E22.right")])]}),"instanceName":"49"});
            var Q50;
            Q50=makeQuery(id+"F10.opRevolve","SWEPT_BODY",BODY,{"disambiguationData":[OSD([sQuery(id+"F9.wireOp",EDGE,"E13"),sQuery(id+"F9.wireOp",EDGE,"E15"),sQuery(id+"F9.wireOp",EDGE,"E16"),sQuery(id+"F9.wireOp",EDGE,"E17")])]});
            booleanBodies(context, id + "F17", {"operationType" : BooleanOperationType.SUBTRACTION, "tools" : qUnion([Q0, Q1, Q2, Q3, Q4, Q5, Q6, Q7, Q8, Q9, Q10, Q11, Q12, Q13, Q14, Q15, Q16, Q17, Q18, Q19, Q20, Q21, Q22, Q23, Q24, Q25, Q26, Q27, Q28, Q29, Q30, Q31, Q32, Q33, Q34, Q35, Q36, Q37, Q38, Q39, Q40, Q41, Q42, Q43, Q44, Q45, Q46, Q47, Q48, Q49]), "targets" : qUnion([Q50])});
        }
        {
            var Q0;
            Q0=makeQuery(id+"F10.opRevolve","SWEPT_BODY",BODY,{"disambiguationData":[OSD([sQuery(id+"F9.wireOp",EDGE,"E13"),sQuery(id+"F9.wireOp",EDGE,"E15"),sQuery(id+"F9.wireOp",EDGE,"E16"),sQuery(id+"F9.wireOp",EDGE,"E17")])]});
            var Q1;
            Q1=qCreatedBy(id+"F11.planeOp",FACE);
            mirror(context, id + "F18", {"entities" : qUnion([Q0]), "mirrorPlane" : qUnion([Q1])});
        }
        {
            var Q0;
            Q0=makeQuery(id+"F8.opExtrude","CAP_EDGE",EDGE,{"disambiguationData":[OSD([sQuery(id+"F7.wireOp",EDGE,"E11")])],"isStart":false});
            var Q1;
            Q1=makeQuery(id+"F8.opExtrude","CAP_EDGE",EDGE,{"disambiguationData":[OSD([sQuery(id+"F7.wireOp",EDGE,"E11")])],"isStart":true});
            chamfer(context, id + "F19", {"entities" : qUnion([Q0, Q1]), "width" : 1 * mm, "tangentPropagation" : true});
        }
    });
